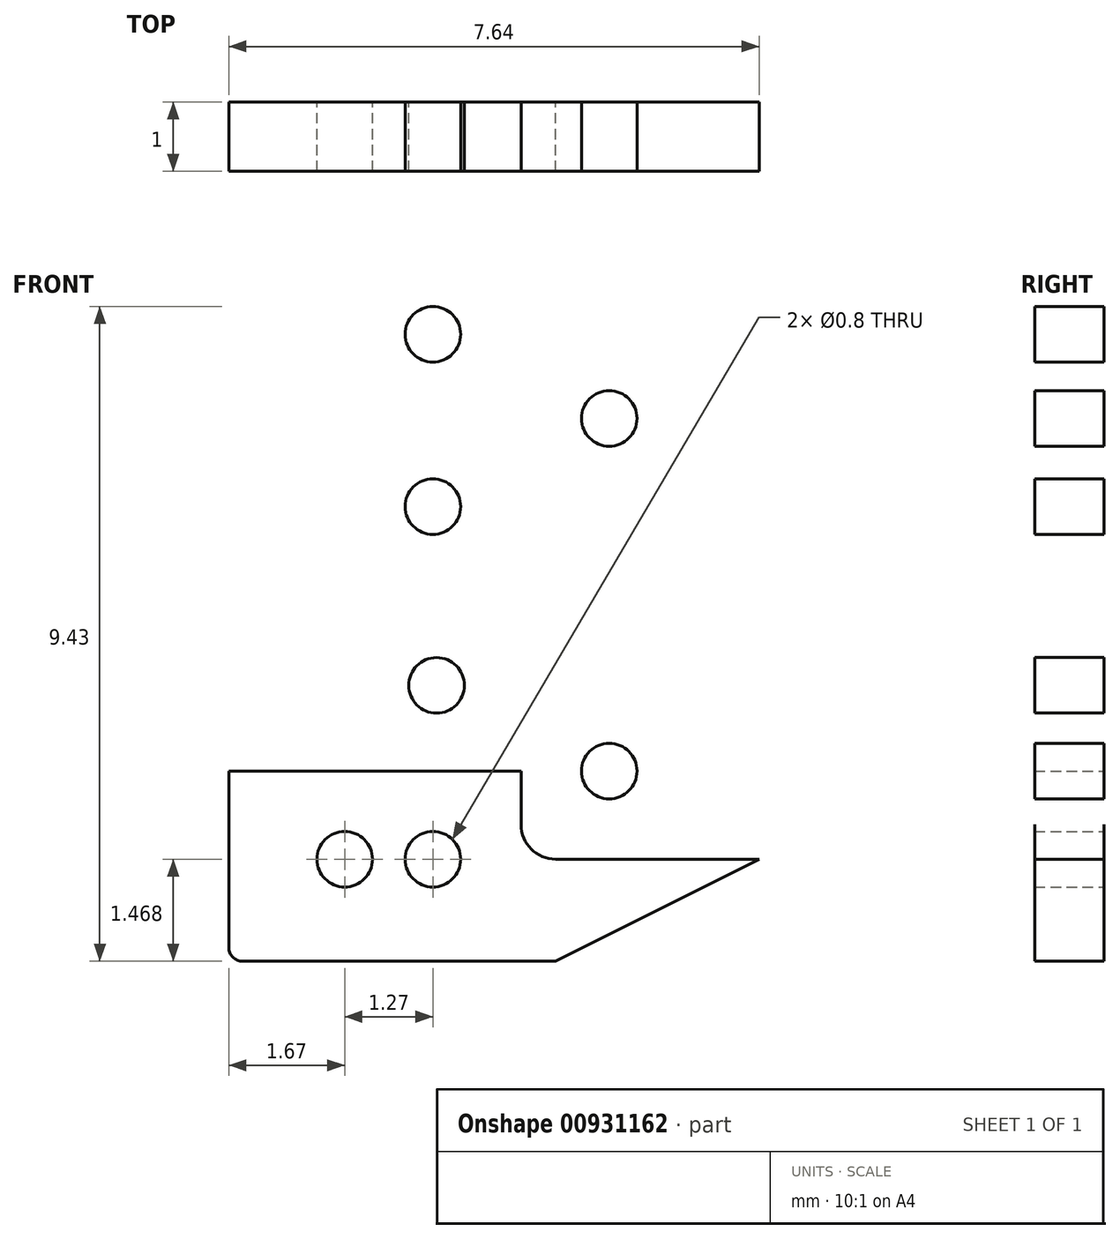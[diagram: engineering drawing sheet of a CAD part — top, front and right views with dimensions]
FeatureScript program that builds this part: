
annotation { "Feature Type Name" : "Feature", "Feature Type Description" : "" }
export const myFeature = defineFeature(function(context is Context, id is Id, definition is map)
    precondition{}
    {
        {
            var Q0;
            Q0=qCreatedBy(makeId("Front.planeOp"),FACE);
            var sketch = newSketch(context, id + "F0", { "sketchPlane" : qUnion([Q0])});
            skCircle(sketch, "E0", {"center": v(-2.54, 3.65) * mm, "radius": 0.4 * mm});
            skCircle(sketch, "E1", {"center": v(-2.54, 1.17) * mm, "radius": 0.4 * mm});
            skCircle(sketch, "E2", {"center": v(-2.49, -1.4) * mm, "radius": 0.4 * mm});
            skCircle(sketch, "E3", {"center": v(0, 2.44) * mm, "radius": 0.4 * mm});
            skCircle(sketch, "E4", {"center": v(0, -2.64) * mm, "radius": 0.4 * mm});
            skCircle(sketch, "E5", {"center": v(3.81, 1.17) * mm, "radius": 0.4 * mm});
            skCircle(sketch, "E6", {"center": v(3.81, -1.37) * mm, "radius": 0.4 * mm});
            skCircle(sketch, "E7", {"center": v(1.27, 2.44) * mm, "radius": 0.4 * mm});
            skCircle(sketch, "E8", {"center": v(1.27, -2.64) * mm, "radius": 0.4 * mm});
            skLineSegment(sketch, "E9", {"start": v(-1.14, 5.36) * mm, "end": v(4.15, 2.71) * mm});
            skArc(sketch, "E10", {"start": v(5.48, 0.57) * mm, "mid": v(5.12, 1.83) * mm, "end": v(4.15, 2.71) * mm});
            skLineSegment(sketch, "E11", {"start": v(5.48, 0.57) * mm, "end": v(5.48, -0.77) * mm});
            skArc(sketch, "E12", {"start": v(4.15, -2.92) * mm, "mid": v(5.12, -2.03) * mm, "end": v(5.48, -0.77) * mm});
            skLineSegment(sketch, "E13", {"start": v(-0.77, -5.38) * mm, "end": v(4.15, -2.92) * mm});
            skLineSegment(sketch, "E14", {"start": v(-5.28, 5.38) * mm, "end": v(-1.23, 5.38) * mm});
            skLineSegment(sketch, "E15", {"start": v(-5.28, -5.38) * mm, "end": v(-0.77, -5.38) * mm});
            skCircle(sketch, "E16", {"center": v(-3.8, 3.7) * mm, "radius": 0.4 * mm});
            skCircle(sketch, "E17", {"center": v(-3.8, 1.17) * mm, "radius": 0.4 * mm});
            skCircle(sketch, "E18", {"center": v(-3.8, -1.37) * mm, "radius": 0.4 * mm});
            skCircle(sketch, "E19", {"center": v(-3.8, -3.91) * mm, "radius": 0.4 * mm});
            skCircle(sketch, "E20", {"center": v(0, -1.37) * mm, "radius": 0.4 * mm});
            skCircle(sketch, "E21", {"center": v(1.27, -1.37) * mm, "radius": 0.4 * mm});
            skCircle(sketch, "E22", {"center": v(0, 1.17) * mm, "radius": 0.4 * mm});
            skCircle(sketch, "E23", {"center": v(1.27, 1.17) * mm, "radius": 0.4 * mm});
            skCircle(sketch, "E24", {"center": v(2.54, 1.17) * mm, "radius": 0.4 * mm});
            skCircle(sketch, "E25", {"center": v(2.54, -1.37) * mm, "radius": 0.4 * mm});
            skLineSegment(sketch, "E26", {"start": v(-5.48, 5.18) * mm, "end": v(-5.48, -5.18) * mm});
            skLineSegment(sketch, "E27", {"start": v(-1.27, 3.2) * mm, "end": v(-1.27, -3.41) * mm});
            skCircle(sketch, "E28", {"center": v(-2.54, -3.91) * mm, "radius": 0.4 * mm});
            skCircle(sketch, "E29", {"center": v(3.13, 2.25) * mm, "radius": 0.4 * mm});
            skCircle(sketch, "E30", {"center": v(3.22, -2.5) * mm, "radius": 0.4 * mm});
            skArc(sketch, "E31", {"start": v(-5.28, 5.38) * mm, "mid": v(-5.42, 5.32) * mm, "end": v(-5.48, 5.18) * mm});
            skArc(sketch, "E32", {"start": v(-5.48, -5.18) * mm, "mid": v(-5.42, -5.32) * mm, "end": v(-5.28, -5.38) * mm});
            skArc(sketch, "E33", {"start": v(-1.14, 5.36) * mm, "mid": v(-1.18, 5.38) * mm, "end": v(-1.23, 5.38) * mm});
            skLineSegment(sketch, "E34", {"start": v(-5.48, 2.44) * mm, "end": v(-1.27, 2.44) * mm});
            skLineSegment(sketch, "E35", {"start": v(-5.48, -2.64) * mm, "end": v(-1.27, -2.64) * mm});
            skLineSegment(sketch, "E36", {"start": v(-5.48, -0.1) * mm, "end": v(5.48, -0.1) * mm});
            skLineSegment(sketch, "E37", {"start": v(-0.77, -3.91) * mm, "end": v(2.16, -3.91) * mm});
            skLineSegment(sketch, "E38", {"start": v(-0.77, 3.7) * mm, "end": v(2.16, 3.7) * mm});
            skArc(sketch, "E39", {"start": v(-1.27, -3.41) * mm, "mid": v(-1.12, -3.77) * mm, "end": v(-0.77, -3.91) * mm});
            skArc(sketch, "E40", {"start": v(-0.77, 3.7) * mm, "mid": v(-1.12, 3.56) * mm, "end": v(-1.27, 3.2) * mm});
            skSolve(sketch);
        }
        {
            var Q0;
            Q0=makeQuery(id+"F0.imprint","IMPRINT",FACE,{"disambiguationData":[TD([[makeQuery(id+"F0.imprint","IMPRINT",EDGE,{"derivedFrom":sQuery(id+"F0.wireOp",EDGE,"E3")}),1.0]])]});
            var Q1;
            Q1=makeQuery(id+"F0.imprint","IMPRINT",FACE,{"disambiguationData":[TD([[makeQuery(id+"F0.imprint","IMPRINT",EDGE,{"derivedFrom":sQuery(id+"F0.wireOp",EDGE,"E0")}),1.0]])]});
            var Q2;
            Q2=makeQuery(id+"F0.imprint","IMPRINT",FACE,{"disambiguationData":[TD([[makeQuery(id+"F0.imprint","IMPRINT",EDGE,{"derivedFrom":sQuery(id+"F0.wireOp",EDGE,"E1")}),1.0]])]});
            var Q3;
            Q3=makeQuery(id+"F0.imprint","IMPRINT",FACE,{"disambiguationData":[TD([[makeQuery(id+"F0.imprint","IMPRINT",EDGE,{"derivedFrom":sQuery(id+"F0.wireOp",EDGE,"E2")}),1.0]])]});
            var Q4;
            {var subQ3=sQuery(id+"F0.wireOp",EDGE,"E15");Q4=makeQuery(id+"F0.imprint","IMPRINT",FACE,{"disambiguationData":[TD([[makeQuery(id+"F0.imprint","IMPRINT",EDGE,{"derivedFrom":subQ3}),1.0]])]});}
            var Q5;
            Q5=makeQuery(id+"F0.imprint","IMPRINT",FACE,{"disambiguationData":[TD([[makeQuery(id+"F0.imprint","IMPRINT",EDGE,{"derivedFrom":sQuery(id+"F0.wireOp",EDGE,"E4")}),1.0]])]});
            extrude(context, id + "F1", {"entities" : qUnion([Q0, Q1, Q2, Q3, Q4, Q5]), "depth" : 1 * mm, "offsetDistance" : 25 * mm});
        }
    });
